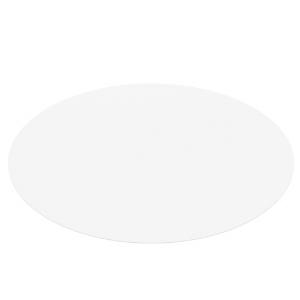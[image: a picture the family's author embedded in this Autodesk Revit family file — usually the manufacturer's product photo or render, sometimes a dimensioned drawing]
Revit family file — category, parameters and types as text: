
# Revit family: sign_110-1380
name_source: partatom
category: Leuchten
revit_build: Autodesk Revit 2016 (Build: 20190508_0715(x64)
units: mm (PartAtom-declared; Revit-internal decimal feet)

## family parameters
Basisbauteil = Fläche
Beim Laden mit Abzugskörper schneiden = Nein
Bemaßung runder Anschluss = Durchmesser verwenden
Gemeinsam genutzt = Nein
Lichtquelle = Nein
Raumberechnungspunkt = Nein
Teiletyp = Normal

## types (1)
- 110-1380-D01-H30 (37 x LED, 436.43 lm, 3.1 W, 3000K)
    Beschreibung = SIGN
    CIE Flux Codes = 47 78 95 100 75
    Color Rendering = 1B/80…89
    Color Temperature = 3000K
    Height = 0 mm  [stored 0 ft]
    Hersteller = Prolicht
    Lamp Light Flux = 436.43 lm
    Lamp Power = 3.1 W
    Lamp count = 37
    Lampe = 37 x LED
    Length = 930 mm
    Luminous efficacy = 105 lm/W
    ModVariant = Nein
    Modell = 110-1380
    Mounting Place = Ceiling
    Mounting Type = Recessed
    Number of Poles = 1
    OnlyDefault = Ja
    Power Factor = 1
    Product Name = SIGN
    Product group = Trimless recessed lights
    ProductGroupID = 411
    Protection Class = Protection class
    Protection Degree = Degree of protection
    RLX_Detail_Level = 1
    RlxData = <blob elided: 60589 chars, md5=ce786b27>
    Scheinlast = 115 VA
    Socket = socket
    Standby Power = 0 W
    System Light Flux = 12062 lm
    System Power = 115 W
    Typenbild = 110-1380.jpg
    Typenkommentare = DIFFUSER Opal (01),LED COLOUR DIR 3000 K (30)
    URL = http://relux.com
    VarID = 110-1380-d01-h30
    Voltage = 0 V
    Vorgabe-Ansicht = 1800 mm
    Weight = 0.00 kg
    Width = 0 mm  [stored 0 ft]

note: [stored X ft] marks values corroborated as IEEE doubles in the binary element streams (Revit-internal decimal feet)

## geometry (parser evidence)
native form markers: Blend x4, Sweep x13
no freeform markers — native parametric forms only
